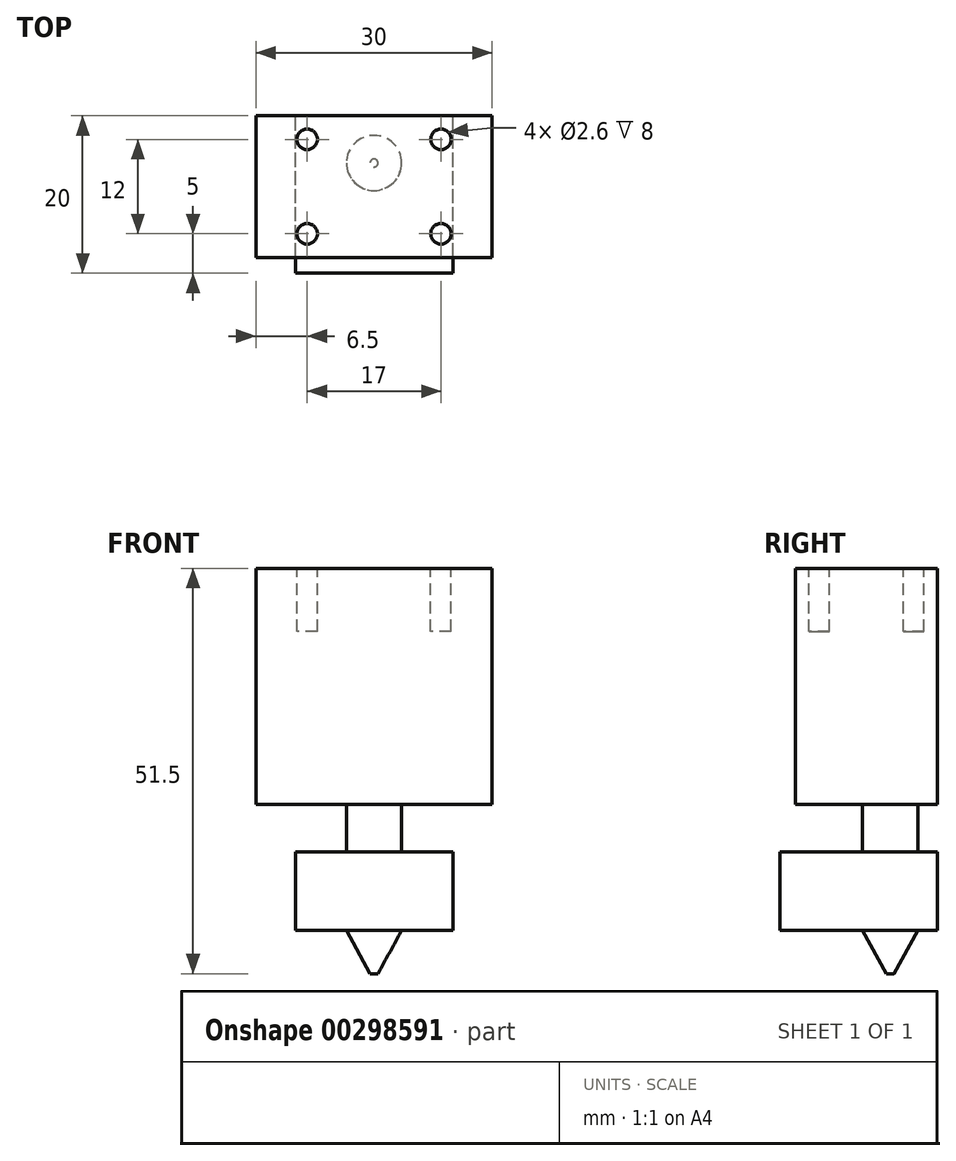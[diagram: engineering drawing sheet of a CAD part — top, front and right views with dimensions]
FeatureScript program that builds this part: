
annotation { "Feature Type Name" : "Feature", "Feature Type Description" : "" }
export const myFeature = defineFeature(function(context is Context, id is Id, definition is map)
    precondition{}
    {
        {
            var Q0;
            Q0=qCreatedBy(makeId("Top.planeOp"),FACE);
            var sketch = newSketch(context, id + "F0", { "sketchPlane" : qUnion([Q0])});
            skLineSegment(sketch, "E0.bottom", {"start": v(15, -9) * mm, "end": v(-15, -9) * mm});
            skLineSegment(sketch, "E0.top", {"start": v(15, 9) * mm, "end": v(-15, 9) * mm});
            skLineSegment(sketch, "E0.left", {"start": v(15, -9) * mm, "end": v(15, 9) * mm});
            skLineSegment(sketch, "E0.right", {"start": v(-15, -9) * mm, "end": v(-15, 9) * mm});
            skPoint(sketch, "E0.middle", {"position": v(0, 0) * mm});
            skSolve(sketch);
        }
        {
            var Q0;
            Q0=makeQuery(id+"F0.imprint","IMPRINT",FACE,{"disambiguationData":[TD([[makeQuery(id+"F0.imprint","IMPRINT",EDGE,{"derivedFrom":sQuery(id+"F0.wireOp",EDGE,"E0.bottom")}),-1.0]])]});
            extrude(context, id + "F1", {"entities" : qUnion([Q0]), "depth" : 30 * mm});
        }
        {
            var Q0;
            Q0=qCreatedBy(makeId("Top.planeOp"),FACE);
            cPlane(context, id + "F2", {"entities" : qUnion([Q0]), "cplaneType" : CPlaneType.OFFSET, "offset" : 6 * mm, "oppositeDirection" : true, "width" : 150 * mm, "height" : 150 * mm});
        }
        {
            var Q0;
            Q0=qCreatedBy(id+"F2.planeOp",FACE);
            var sketch = newSketch(context, id + "F3", { "sketchPlane" : qUnion([Q0])});
            skLineSegment(sketch, "E1.bottom", {"start": v(-10, -11) * mm, "end": v(10, -11) * mm});
            skLineSegment(sketch, "E1.top", {"start": v(-10, 9) * mm, "end": v(10, 9) * mm});
            skLineSegment(sketch, "E1.left", {"start": v(-10, -11) * mm, "end": v(-10, 9) * mm});
            skLineSegment(sketch, "E1.right", {"start": v(10, -11) * mm, "end": v(10, 9) * mm});
            skSolve(sketch);
        }
        {
            var Q0;
            Q0=makeQuery(id+"F1.opExtrude","CAP_FACE",FACE,{"disambiguationData":[OSD([sQuery(id+"F0.wireOp",EDGE,"E0.bottom"),sQuery(id+"F0.wireOp",EDGE,"E0.top"),sQuery(id+"F0.wireOp",EDGE,"E0.left"),sQuery(id+"F0.wireOp",EDGE,"E0.right")])],"isStart":false});
            var sketch = newSketch(context, id + "F4", { "sketchPlane" : qUnion([Q0])});
            skCircle(sketch, "E2", {"center": v(0, 3) * mm, "radius": 3.5 * mm});
            skSolve(sketch);
        }
        {
            var Q0;
            Q0=qSketchRegion(id+"F3",true);
            extrude(context, id + "F5", {"entities" : qUnion([Q0]), "operationType" : NewBodyOperationType.ADD, "oppositeDirection" : true, "depth" : 10 * mm});
        }
        {
            var Q0;
            Q0=qSketchRegion(id+"F4",true);
            var Q1;
            Q1=makeQuery(id+"F5.opExtrude","CAP_FACE",FACE,{"disambiguationData":[OSD([sQuery(id+"F3.wireOp",EDGE,"E1.bottom"),sQuery(id+"F3.wireOp",EDGE,"E1.top"),sQuery(id+"F3.wireOp",EDGE,"E1.left"),sQuery(id+"F3.wireOp",EDGE,"E1.right")])],"isStart":false});
            extrude(context, id + "F6", {"entities" : qUnion([Q0]), "operationType" : NewBodyOperationType.ADD, "endBound" : BoundingType.UP_TO_SURFACE, "oppositeDirection" : true, "endBoundEntityFace" : qUnion([Q1]), "depth" : 25 * mm});
        }
        {
            var Q0;
            Q0=makeQuery(id+"F5.opExtrude","CAP_FACE",FACE,{"disambiguationData":[OSD([sQuery(id+"F3.wireOp",EDGE,"E1.bottom"),sQuery(id+"F3.wireOp",EDGE,"E1.top"),sQuery(id+"F3.wireOp",EDGE,"E1.left"),sQuery(id+"F3.wireOp",EDGE,"E1.right")])],"isStart":false});
            var sketch = newSketch(context, id + "F7", { "sketchPlane" : qUnion([Q0])});
            skCircle(sketch, "E3.0", {"center": v(0, -3) * mm, "radius": 3.5 * mm});
            skSolve(sketch);
        }
        {
            var Q0;
            Q0=makeQuery(id+"F1.opExtrude","CAP_FACE",FACE,{"disambiguationData":[OSD([sQuery(id+"F0.wireOp",EDGE,"E0.bottom"),sQuery(id+"F0.wireOp",EDGE,"E0.top"),sQuery(id+"F0.wireOp",EDGE,"E0.left"),sQuery(id+"F0.wireOp",EDGE,"E0.right")])],"isStart":false});
            cPlane(context, id + "F8", {"entities" : qUnion([Q0]), "cplaneType" : CPlaneType.OFFSET, "offset" : (56 - 4.5) * mm, "oppositeDirection" : true, "width" : 150 * mm, "height" : 150 * mm});
        }
        {
            var Q0;
            Q0=qCreatedBy(id+"F8.planeOp",FACE);
            var sketch = newSketch(context, id + "F9", { "sketchPlane" : qUnion([Q0])});
            skCircle(sketch, "E4", {"center": v(0, 3) * mm, "radius": 0.5 * mm});
            skSolve(sketch);
        }
        {
            var Q1;
            Q1=qSketchRegion(id+"F9",true);
            var Q2;
            Q2=qSketchRegion(id+"F7",true);
            loft(context, id + "F10", {"operationType" : NewBodyOperationType.ADD, "sheetProfilesArray" : [{ "sheetProfileEntities" : qUnion([Q1]) }, { "sheetProfileEntities" : qUnion([Q2]) }]});
        }
        {
            var Q0;
            Q0=makeQuery(id+"F1.opExtrude","CAP_FACE",FACE,{"disambiguationData":[OSD([sQuery(id+"F0.wireOp",EDGE,"E0.bottom"),sQuery(id+"F0.wireOp",EDGE,"E0.top"),sQuery(id+"F0.wireOp",EDGE,"E0.left"),sQuery(id+"F0.wireOp",EDGE,"E0.right")])],"isStart":false});
            var sketch = newSketch(context, id + "F11", { "sketchPlane" : qUnion([Q0])});
            skCircle(sketch, "E5", {"center": v(-8.5, 6) * mm, "radius": 1.3 * mm});
            skCircle(sketch, "E6", {"center": v(8.5, 6) * mm, "radius": 1.3 * mm});
            skCircle(sketch, "E7", {"center": v(8.5, -6) * mm, "radius": 1.3 * mm});
            skCircle(sketch, "E8", {"center": v(-8.5, -6) * mm, "radius": 1.3 * mm});
            skSolve(sketch);
        }
        {
            var Q0;
            Q0=qSketchRegion(id+"F11",true);
            extrude(context, id + "F12", {"entities" : qUnion([Q0]), "operationType" : NewBodyOperationType.REMOVE, "oppositeDirection" : true, "depth" : 8 * mm});
        }
    });
